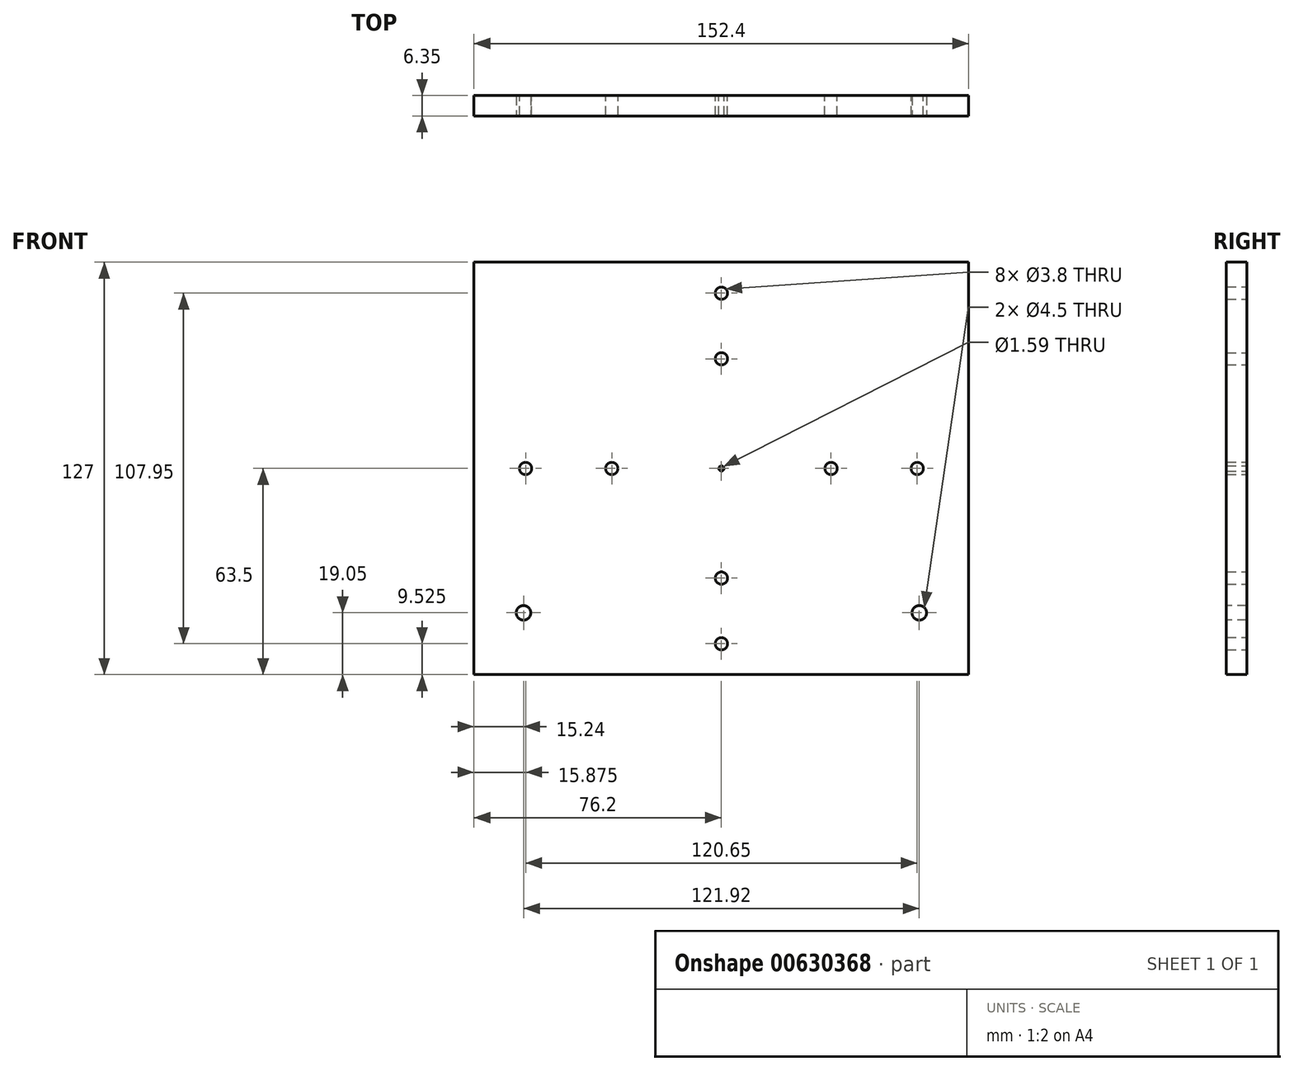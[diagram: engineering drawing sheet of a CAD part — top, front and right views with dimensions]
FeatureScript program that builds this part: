
annotation { "Feature Type Name" : "Feature", "Feature Type Description" : "" }
export const myFeature = defineFeature(function(context is Context, id is Id, definition is map)
    precondition{}
    {
        {
            var Q0;
            Q0=qCreatedBy(makeId("Front.planeOp"),FACE);
            var sketch = newSketch(context, id + "F0", { "sketchPlane" : qUnion([Q0])});
            skCircle(sketch, "E0", {"center": v(0, 0) * mm, "radius": 0.8 * mm});
            skLineSegment(sketch, "E1.bottom", {"start": v(-76.2, 63.5) * mm, "end": v(76.2, 63.5) * mm});
            skLineSegment(sketch, "E1.top", {"start": v(-76.2, -63.5) * mm, "end": v(76.2, -63.5) * mm});
            skLineSegment(sketch, "E1.left", {"start": v(-76.2, 63.5) * mm, "end": v(-76.2, -63.5) * mm});
            skLineSegment(sketch, "E1.right", {"start": v(76.2, 63.5) * mm, "end": v(76.2, -63.5) * mm});
            skSolve(sketch);
        }
        {
            var Q0;
            Q0 = qSketchRegion(id + "F0", true);
            extrude(context, id + "F1", {"entities" : qUnion([Q0]), "depth" : 6.35 * mm, "offsetDistance" : 25.4 * mm});
        }
        {
            var Q0;
            Q0=makeQuery(id+"F1.opExtrude","CAP_FACE",FACE,{"disambiguationData":[OSD([sQuery(id+"F0.wireOp",EDGE,"E0"),sQuery(id+"F0.wireOp",EDGE,"E1.bottom"),sQuery(id+"F0.wireOp",EDGE,"E1.top"),sQuery(id+"F0.wireOp",EDGE,"E1.left"),sQuery(id+"F0.wireOp",EDGE,"E1.right")])],"isStart":true});
            var sketch = newSketch(context, id + "F2", { "sketchPlane" : qUnion([Q0])});
            skCircle(sketch, "E2", {"center": v(0, 0) * mm, "radius": 38.96 * mm});
            skCircle(sketch, "E3", {"center": v(0, 0) * mm, "radius": 28.58 * mm});
            skLineSegment(sketch, "E4", {"start": v(-38.96, 0) * mm, "end": v(-28.58, 0) * mm, "construction": true});
            skLineSegment(sketch, "E5", {"start": v(28.58, 0) * mm, "end": v(38.96, 0) * mm, "construction": true});
            skLineSegment(sketch, "E6", {"start": v(0, 38.96) * mm, "end": v(0, 28.58) * mm, "construction": true});
            skLineSegment(sketch, "E7", {"start": v(0, -38.96) * mm, "end": v(0, -28.58) * mm, "construction": true});
            skPoint(sketch, "E8", {"position": v(0, 33.77) * mm});
            skPoint(sketch, "E9", {"position": v(33.77, 0) * mm});
            skPoint(sketch, "E10", {"position": v(0, -33.77) * mm});
            skPoint(sketch, "E11", {"position": v(-33.77, 0) * mm});
            skSolve(sketch);
        }
        {
            var Q0;
            Q0=sQuery(id+"F2.wireOp",VERTEX,"E8");
            var Q1;
            Q1=sQuery(id+"F2.wireOp",VERTEX,"E9");
            var Q2;
            Q2=sQuery(id+"F2.wireOp",VERTEX,"E11");
            var Q3;
            Q3=sQuery(id+"F2.wireOp",VERTEX,"E10");
            var Q4;
            Q4=makeQuery(id+"F1.opExtrude","SWEPT_BODY",BODY,{"disambiguationData":[OSD([sQuery(id+"F0.wireOp",EDGE,"E0"),sQuery(id+"F0.wireOp",EDGE,"E1.bottom"),sQuery(id+"F0.wireOp",EDGE,"E1.top"),sQuery(id+"F0.wireOp",EDGE,"E1.left"),sQuery(id+"F0.wireOp",EDGE,"E1.right")])]});
            hole(context, id + "F3", {"style" : HoleStyle.SIMPLE, "endStyle" : HoleEndStyle.THROUGH, "standardTappedOrClearance" : lookupTablePath({ "standard" : "ANSI", "fit" : "Normal (ASME)", "size" : "#6", "type" : "Clearance" }), "standardBlindInLast" : lookupTablePath({ "fit" : "Free", "standard" : "ANSI", "size" : "#6", "type" : "Clearance" }), "holeDiameter" : 3.8 * mm, "majorDiameter" : 6.35 * mm, "isTappedThrough" : true, "tappedDepth" : 12.7 * mm, "tapClearance" : 3, "locations" : qUnion([Q0, Q1, Q2, Q3]), "scope" : qUnion([Q4])});
        }
        {
            var Q0;
            Q0=makeQuery(id+"F1.opExtrude","CAP_FACE",FACE,{"disambiguationData":[OSD([sQuery(id+"F0.wireOp",EDGE,"E0"),sQuery(id+"F0.wireOp",EDGE,"E1.bottom"),sQuery(id+"F0.wireOp",EDGE,"E1.top"),sQuery(id+"F0.wireOp",EDGE,"E1.left"),sQuery(id+"F0.wireOp",EDGE,"E1.right")])],"isStart":true});
            var sketch = newSketch(context, id + "F4", { "sketchPlane" : qUnion([Q0])});
            skCircle(sketch, "E12", {"center": v(0, 0) * mm, "radius": 44.45 * mm, "construction": true});
            skLineSegment(sketch, "E13", {"start": v(0, 44.45) * mm, "end": v(0, 63.5) * mm, "construction": true});
            skLineSegment(sketch, "E14", {"start": v(44.45, 0) * mm, "end": v(76.2, 0) * mm, "construction": true});
            skLineSegment(sketch, "E15", {"start": v(0, -44.45) * mm, "end": v(0, -63.5) * mm, "construction": true});
            skLineSegment(sketch, "E16", {"start": v(-44.45, 0) * mm, "end": v(-76.2, 0) * mm, "construction": true});
            skPoint(sketch, "E17", {"position": v(0, 53.98) * mm});
            skPoint(sketch, "E18", {"position": v(60.33, 0) * mm});
            skPoint(sketch, "E19", {"position": v(0, -53.97) * mm});
            skPoint(sketch, "E20", {"position": v(-60.33, 0) * mm});
            skSolve(sketch);
        }
        {
            var Q0;
            Q0=sQuery(id+"F4.wireOp",VERTEX,"E17");
            var Q1;
            Q1=sQuery(id+"F4.wireOp",VERTEX,"E18");
            var Q2;
            Q2=sQuery(id+"F4.wireOp",VERTEX,"E19");
            var Q3;
            Q3=sQuery(id+"F4.wireOp",VERTEX,"E20");
            var Q4;
            Q4=makeQuery(id+"F1.opExtrude","SWEPT_BODY",BODY,{"disambiguationData":[OSD([sQuery(id+"F0.wireOp",EDGE,"E0"),sQuery(id+"F0.wireOp",EDGE,"E1.bottom"),sQuery(id+"F0.wireOp",EDGE,"E1.top"),sQuery(id+"F0.wireOp",EDGE,"E1.left"),sQuery(id+"F0.wireOp",EDGE,"E1.right")])]});
            hole(context, id + "F5", {"style" : HoleStyle.SIMPLE, "endStyle" : HoleEndStyle.THROUGH, "standardTappedOrClearance" : lookupTablePath({ "standard" : "ANSI", "fit" : "Normal (ASME)", "size" : "#6", "type" : "Clearance" }), "standardBlindInLast" : lookupTablePath({ "fit" : "Free", "standard" : "ANSI", "size" : "#6", "type" : "Clearance" }), "holeDiameter" : 3.8 * mm, "majorDiameter" : 6.35 * mm, "isTappedThrough" : true, "tappedDepth" : 12.7 * mm, "tapClearance" : 3, "locations" : qUnion([Q0, Q1, Q2, Q3]), "scope" : qUnion([Q4])});
        }
        {
            var Q0;
            Q0=makeQuery(id+"F1.opExtrude","CAP_FACE",FACE,{"disambiguationData":[OSD([sQuery(id+"F0.wireOp",EDGE,"E0"),sQuery(id+"F0.wireOp",EDGE,"E1.bottom"),sQuery(id+"F0.wireOp",EDGE,"E1.top"),sQuery(id+"F0.wireOp",EDGE,"E1.left"),sQuery(id+"F0.wireOp",EDGE,"E1.right")])],"isStart":true});
            var sketch = newSketch(context, id + "F6", { "sketchPlane" : qUnion([Q0])});
            skPoint(sketch, "E21", {"position": v(-44.45, -63.5) * mm});
            skPoint(sketch, "E22", {"position": v(44.45, -63.5) * mm});
            skLineSegment(sketch, "E23", {"start": v(-44.45, -63.5) * mm, "end": v(44.45, -63.5) * mm, "construction": true});
            skLineSegment(sketch, "E24", {"start": v(76.2, -63.5) * mm, "end": v(44.45, -63.5) * mm, "construction": true});
            skLineSegment(sketch, "E25", {"start": v(-44.45, -63.5) * mm, "end": v(-76.2, -63.5) * mm, "construction": true});
            skSolve(sketch);
        }
        {
            var Q0;
            Q0=makeQuery(id+"F1.opExtrude","CAP_FACE",FACE,{"disambiguationData":[OSD([sQuery(id+"F0.wireOp",EDGE,"E0"),sQuery(id+"F0.wireOp",EDGE,"E1.bottom"),sQuery(id+"F0.wireOp",EDGE,"E1.top"),sQuery(id+"F0.wireOp",EDGE,"E1.left"),sQuery(id+"F0.wireOp",EDGE,"E1.right")])],"isStart":false});
            var sketch = newSketch(context, id + "F7", { "sketchPlane" : qUnion([Q0])});
            skLineSegment(sketch, "E26", {"start": v(-44.45, -44.45) * mm, "end": v(-44.45, -63.5) * mm, "construction": true});
            skLineSegment(sketch, "E27", {"start": v(44.45, -44.45) * mm, "end": v(44.45, -63.5) * mm, "construction": true});
            skLineSegment(sketch, "E28", {"start": v(-44.45, -44.45) * mm, "end": v(-60.96, -44.45) * mm, "construction": true});
            skLineSegment(sketch, "E29", {"start": v(44.45, -44.45) * mm, "end": v(60.96, -44.45) * mm, "construction": true});
            skPoint(sketch, "E30", {"position": v(60.96, -44.45) * mm});
            skPoint(sketch, "E31", {"position": v(-60.96, -44.45) * mm});
            skSolve(sketch);
        }
        {
            var Q0;
            Q0=sQuery(id+"F7.wireOp",VERTEX,"E31");
            var Q1;
            Q1=sQuery(id+"F7.wireOp",VERTEX,"E30");
            var Q2;
            Q2=makeQuery(id+"F1.opExtrude","SWEPT_BODY",BODY,{"disambiguationData":[OSD([sQuery(id+"F0.wireOp",EDGE,"E0"),sQuery(id+"F0.wireOp",EDGE,"E1.bottom"),sQuery(id+"F0.wireOp",EDGE,"E1.top"),sQuery(id+"F0.wireOp",EDGE,"E1.left"),sQuery(id+"F0.wireOp",EDGE,"E1.right")])]});
            hole(context, id + "F8", {"style" : HoleStyle.SIMPLE, "endStyle" : HoleEndStyle.THROUGH, "standardTappedOrClearance" : lookupTablePath({ "standard" : "ANSI", "fit" : "Normal (ASME)", "size" : "#8", "type" : "Clearance" }), "standardBlindInLast" : lookupTablePath({ "fit" : "Free", "standard" : "ANSI", "size" : "#8", "type" : "Clearance" }), "holeDiameter" : 4.5 * mm, "majorDiameter" : 6.35 * mm, "isTappedThrough" : true, "tappedDepth" : 12.7 * mm, "tapClearance" : 3, "locations" : qUnion([Q0, Q1]), "scope" : qUnion([Q2])});
        }
    });
